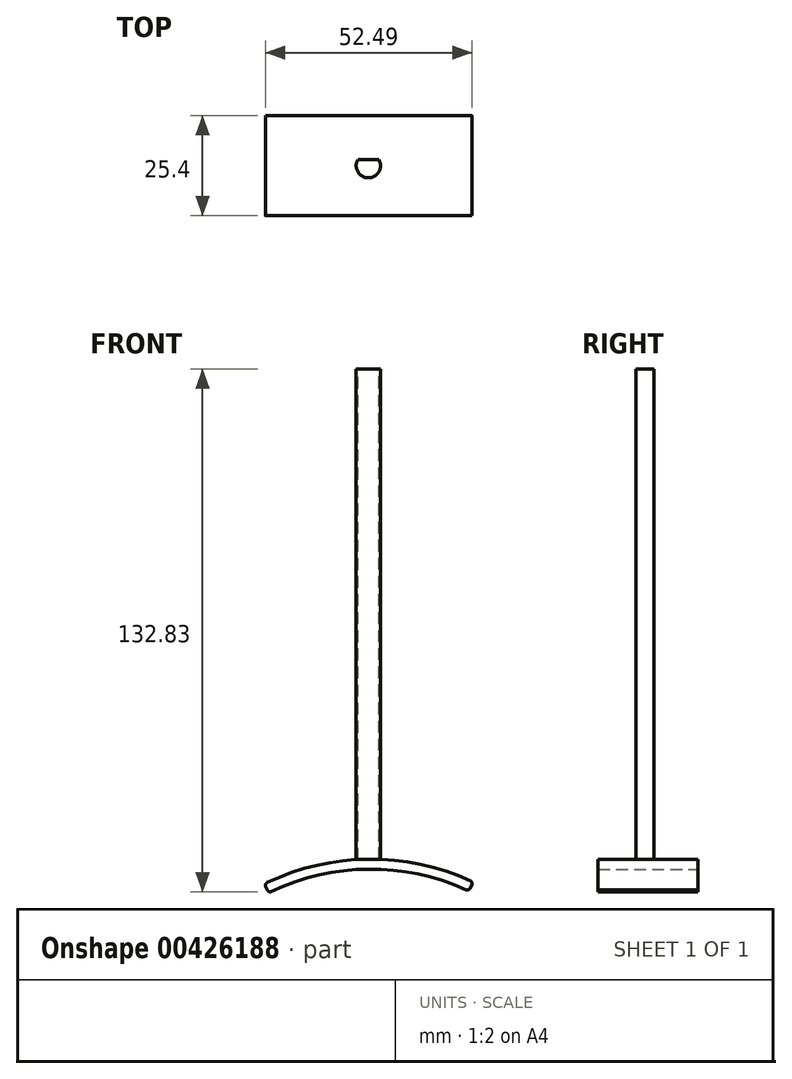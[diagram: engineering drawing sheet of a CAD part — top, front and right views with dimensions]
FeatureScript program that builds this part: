
annotation { "Feature Type Name" : "Feature", "Feature Type Description" : "" }
export const myFeature = defineFeature(function(context is Context, id is Id, definition is map)
    precondition{}
    {
        {
            var Q0;
            Q0=qCreatedBy(makeId("Front.planeOp"),FACE);
            var sketch = newSketch(context, id + "F0", { "sketchPlane" : qUnion([Q0])});
            skLineSegment(sketch, "E0.bottom", {"start": v(3.09, 63.5) * mm, "end": v(-3.09, 63.5) * mm});
            skLineSegment(sketch, "E0.top", {"start": v(3.09, -63.5) * mm, "end": v(-3.09, -63.5) * mm});
            skLineSegment(sketch, "E0.left", {"start": v(3.09, 63.5) * mm, "end": v(3.09, -63.5) * mm});
            skLineSegment(sketch, "E0.right", {"start": v(-3.09, 63.5) * mm, "end": v(-3.09, -63.5) * mm});
            skPoint(sketch, "E0.middle", {"position": v(0, 0) * mm});
            skLineSegment(sketch, "E1", {"start": v(0, 63.5) * mm, "end": v(0, -63.5) * mm});
            skSolve(sketch);
        }
        {
            var Q0;
            {var subQ0=sQuery(id+"F0.wireOp",EDGE,"E0.left");Q0=makeQuery(id+"F0.imprint","IMPRINT",FACE,{"disambiguationData":[TD([[makeQuery(id+"F0.imprint","IMPRINT",EDGE,{"derivedFrom":subQ0}),-1.0]])]});}
            var Q1;
            Q1=sQuery(id+"F0.wireOp",EDGE,"E1");
            revolve(context, id + "F1", {"entities" : qUnion([Q0]), "axis" : qUnion([Q1]), "revolveType" : RevolveType.FULL});
        }
        {
            var Q0;
            Q0=makeQuery(id+"F1.opRevolve","SWEPT_FACE",FACE,{"disambiguationData":[OSD([sQuery(id+"F0.wireOp",EDGE,"E0.bottom")])]});
            var sketch = newSketch(context, id + "F2", { "sketchPlane" : qUnion([Q0])});
            skCircle(sketch, "E2", {"center": v(0, 0) * mm, "radius": 3.09 * mm});
            skLineSegment(sketch, "E3", {"start": v(-2.66, 1.56) * mm, "end": v(2.66, 1.56) * mm});
            skPoint(sketch, "E4", {"position": v(0, -3.09) * mm});
            skSolve(sketch);
        }
        {
            var Q0;
            {var subQ0=sQuery(id+"F2.wireOp",EDGE,"E3");Q0=makeQuery(id+"F2.imprint","IMPRINT",FACE,{"disambiguationData":[TD([[makeQuery(id+"F2.imprint","IMPRINT",EDGE,{"derivedFrom":subQ0}),1.0]])]});}
            extrude(context, id + "F3", {"entities" : qUnion([Q0]), "operationType" : NewBodyOperationType.REMOVE, "oppositeDirection" : true, "depth" : 150.22 * mm});
        }
        {
            var Q0;
            Q0=qCreatedBy(makeId("Front.planeOp"),FACE);
            var sketch = newSketch(context, id + "F4", { "sketchPlane" : qUnion([Q0])});
            skArc(sketch, "E5", {"start": v(24.84, -68.8) * mm, "mid": v(0.07, -63.55) * mm, "end": v(-24.6, -69.25) * mm});
            skArc(sketch, "E6.0", {"start": v(25.9, -66.5) * mm, "mid": v(0.05, -61.01) * mm, "end": v(-25.7, -66.96) * mm});
            skLineSegment(sketch, "E7", {"start": v(-25.61, -68.9) * mm, "end": v(-26.06, -67.99) * mm});
            skLineSegment(sketch, "E8", {"start": v(25.84, -68.43) * mm, "end": v(26.27, -67.51) * mm});
            skPoint(sketch, "E9.visualSharp", {"position": v(-26.4, -67.3) * mm});
            skArc(sketch, "E9.filletArc", {"start": v(-25.7, -66.96) * mm, "mid": v(-26.1, -67.4) * mm, "end": v(-26.06, -67.99) * mm});
            skPoint(sketch, "E10.visualSharp", {"position": v(-25.28, -69.58) * mm});
            skArc(sketch, "E10.filletArc", {"start": v(-25.61, -68.9) * mm, "mid": v(-25.18, -69.28) * mm, "end": v(-24.6, -69.25) * mm});
            skPoint(sketch, "E11.visualSharp", {"position": v(25.52, -69.12) * mm});
            skArc(sketch, "E11.filletArc", {"start": v(24.84, -68.8) * mm, "mid": v(25.42, -68.82) * mm, "end": v(25.84, -68.43) * mm});
            skPoint(sketch, "E12.visualSharp", {"position": v(26.6, -66.82) * mm});
            skArc(sketch, "E12.filletArc", {"start": v(26.27, -67.51) * mm, "mid": v(26.3, -66.92) * mm, "end": v(25.9, -66.5) * mm});
            skSolve(sketch);
        }
        {
            var Q0;
            Q0 = qSketchRegion(id + "F4", true);
            extrude(context, id + "F5", {"entities" : qUnion([Q0]), "operationType" : NewBodyOperationType.ADD, "endBound" : BoundingType.SYMMETRIC, "depth" : 25.4 * mm});
        }
    });
